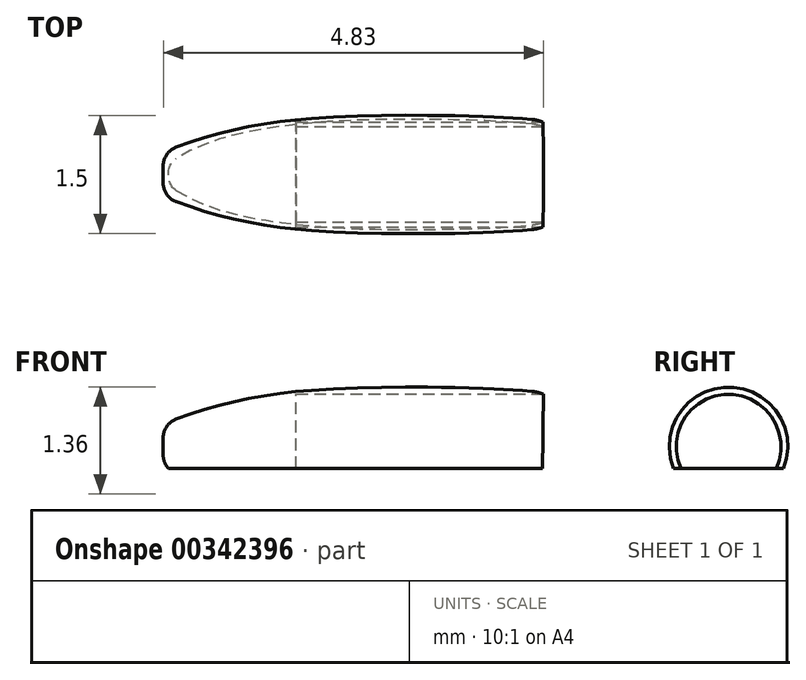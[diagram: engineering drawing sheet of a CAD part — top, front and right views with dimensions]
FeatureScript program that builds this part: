
annotation { "Feature Type Name" : "Feature", "Feature Type Description" : "" }
export const myFeature = defineFeature(function(context is Context, id is Id, definition is map)
    precondition{}
    {
        {
            var Q0;
            Q0=qCreatedBy(makeId("Front.planeOp"),FACE);
            var sketch = newSketch(context, id + "F0", { "sketchPlane" : qUnion([Q0])});
            skFitSpline(sketch, "E0", {"points": [v(58.46, 31.32) * mm, v(59.33, 31.6) * mm, v(60.23, 31.74) * mm, v(61.35, 31.79) * mm, v(62.75, 31.76) * mm, v(63.6, 31.68) * mm], "startDerivative": vector(4.55, 1.81) * mm, "endDerivative": vector(4.3, -0.7) * mm});
            skLineSegment(sketch, "E1", {"start": v(63.6, 31.68) * mm, "end": v(63.6, 31.04) * mm});
            skLineSegment(sketch, "E2", {"start": v(63.6, 31.04) * mm, "end": v(58.46, 31.04) * mm});
            skLineSegment(sketch, "E3", {"start": v(58.46, 31.04) * mm, "end": v(58.46, 31.14) * mm});
            skLineSegment(sketch, "E4", {"start": v(58.35, 31.04) * mm, "end": v(63.75, 31.04) * mm});
            skArc(sketch, "E5.filletArc", {"start": v(58.62, 31.38) * mm, "mid": v(58.5, 31.29) * mm, "end": v(58.46, 31.14) * mm});
            skSolve(sketch);
        }
        {
            var Q0;
            Q0 = qSketchRegion(id + "F0", true);
            var Q1;
            Q1=sQuery(id+"F0.wireOp",EDGE,"E4");
            revolve(context, id + "F1", {"entities" : qUnion([Q0]), "axis" : qUnion([Q1]), "revolveType" : RevolveType.FULL});
        }
        {
            var Q0;
            Q0=makeQuery(id+"F1.opRevolve","SWEPT_EDGE",EDGE,{"disambiguationData":[OSD([sQuery(id+"F0.wireOp",EDGE,"E0"),sQuery(id+"F0.wireOp",EDGE,"E1")])]});
            fillet(context, id + "F2", {"entities" : qUnion([Q0]), "radius" : 0.5 * mm, "tangentPropagation" : true, "allowEdgeOverflow" : false});
        }
        {
            var Q0;
            Q0=qCreatedBy(makeId("Right.planeOp"),FACE);
            cPlane(context, id + "F3", {"entities" : qUnion([Q0]), "cplaneType" : CPlaneType.OFFSET, "offset" : 110.74 * mm, "width" : 152.4 * mm, "height" : 152.4 * mm});
        }
        {
            var Q0;
            Q0=qCreatedBy(id+"F3.planeOp",FACE);
            var sketch = newSketch(context, id + "F4", { "sketchPlane" : qUnion([Q0])});
            skCircle(sketch, "E6", {"center": v(0, 31.03) * mm, "radius": 0.67 * mm});
            skSolve(sketch);
        }
        {
            var Q0;
            Q0 = qSketchRegion(id + "F4", true);
            extrude(context, id + "F5", {"entities" : qUnion([Q0]), "operationType" : NewBodyOperationType.REMOVE, "oppositeDirection" : true, "depth" : 50.6 * mm});
        }
        {
            var Q0;
            Q0=qCreatedBy(id+"F3.planeOp",FACE);
            var sketch = newSketch(context, id + "F6", { "sketchPlane" : qUnion([Q0])});
            skLineSegment(sketch, "E7", {"start": v(-0.74, 30.76) * mm, "end": v(0.88, 30.76) * mm});
            skLineSegment(sketch, "E8", {"start": v(-0.74, 30.76) * mm, "end": v(-0.74, 30.13) * mm});
            skLineSegment(sketch, "E9", {"start": v(-0.74, 30.13) * mm, "end": v(0.86, 30.13) * mm});
            skLineSegment(sketch, "E10", {"start": v(0.86, 30.13) * mm, "end": v(0.88, 30.76) * mm});
            skSolve(sketch);
        }
        {
            var Q0;
            Q0 = qSketchRegion(id + "F6", true);
            extrude(context, id + "F7", {"entities" : qUnion([Q0]), "operationType" : NewBodyOperationType.REMOVE, "oppositeDirection" : true, "depth" : 65.53 * mm});
        }
    });
